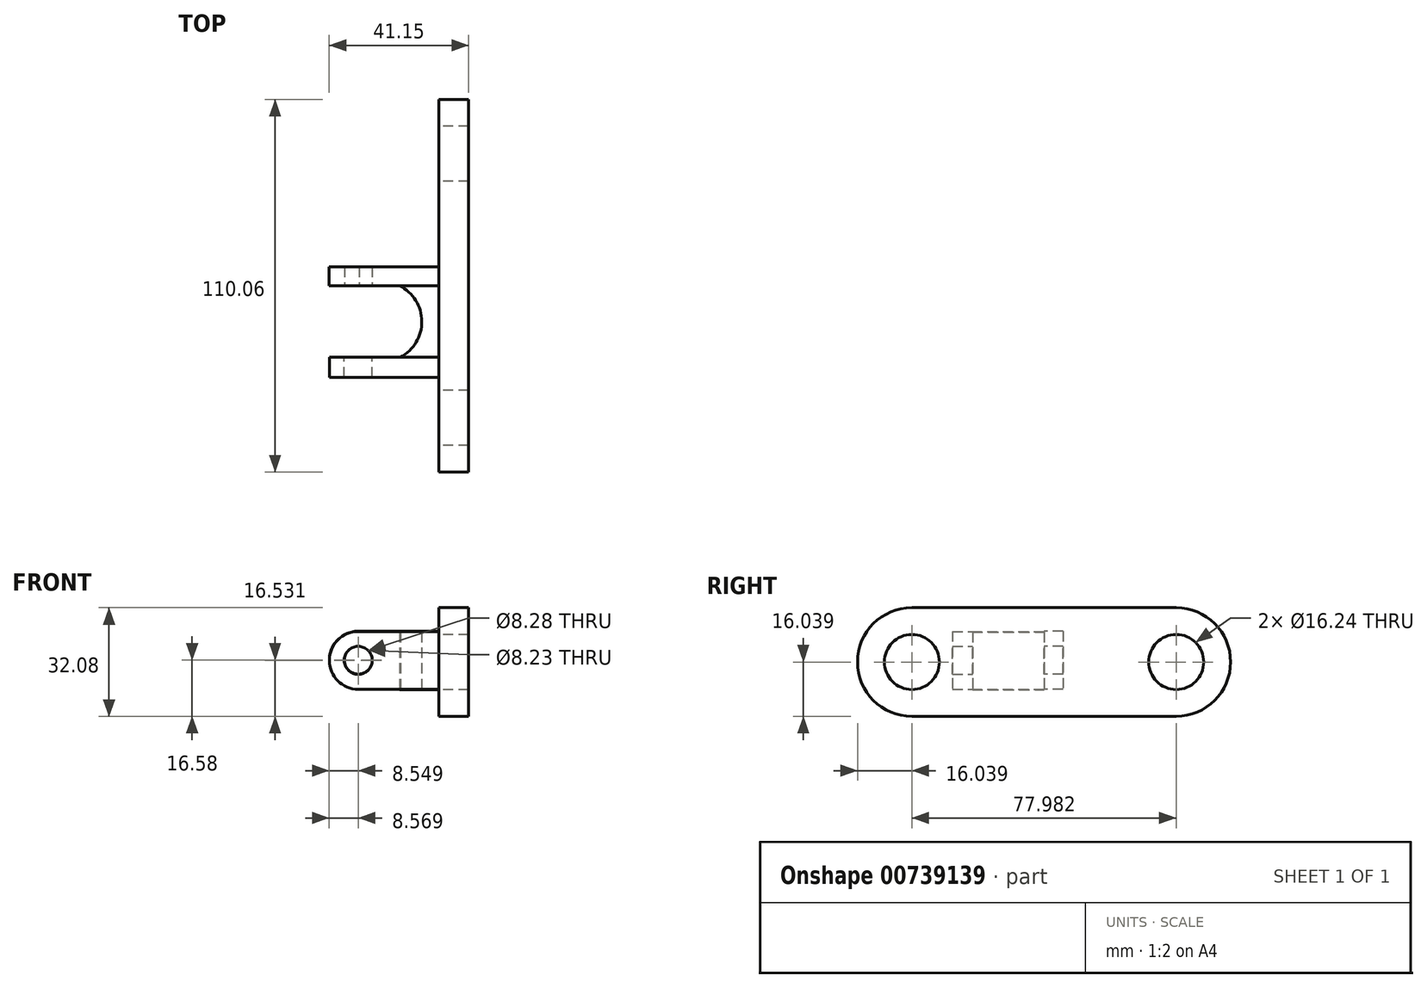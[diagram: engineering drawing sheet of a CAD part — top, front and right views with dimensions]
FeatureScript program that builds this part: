
annotation { "Feature Type Name" : "Feature", "Feature Type Description" : "" }
export const myFeature = defineFeature(function(context is Context, id is Id, definition is map)
    precondition{}
    {
        {
            var Q0;
            Q0=qCreatedBy(makeId("Right.planeOp"),FACE);
            var sketch = newSketch(context, id + "F0", { "sketchPlane" : qUnion([Q0])});
            skLineSegment(sketch, "E0", {"start": v(0, -16.5) * mm, "end": v(39, -16.5) * mm});
            skLineSegment(sketch, "E1", {"start": v(0, -16.5) * mm, "end": v(-39, -16.5) * mm});
            skLineSegment(sketch, "E2", {"start": v(39, 15.58) * mm, "end": v(-39, 15.58) * mm});
            skArc(sketch, "E3", {"start": v(39, -16.5) * mm, "mid": v(55.03, -0.46) * mm, "end": v(39, 15.58) * mm});
            skArc(sketch, "E4", {"start": v(-39, 15.58) * mm, "mid": v(-55.03, -0.46) * mm, "end": v(-39, -16.5) * mm});
            skCircle(sketch, "E5", {"center": v(39, -0.46) * mm, "radius": 8.12 * mm});
            skCircle(sketch, "E6", {"center": v(-39, -0.46) * mm, "radius": 8.12 * mm});
            skSolve(sketch);
        }
        {
            var Q0;
            Q0=makeQuery(id+"F0.imprint","IMPRINT",FACE,{"disambiguationData":[TD([[makeQuery(id+"F0.imprint","IMPRINT",EDGE,{"derivedFrom":sQuery(id+"F0.wireOp",EDGE,"E0")}),1.0]])]});
            extrude(context, id + "F1", {"entities" : qUnion([Q0]), "depth" : 8.9 * mm, "offsetDistance" : 25.4 * mm});
        }
        {
            var Q0;
            Q0=qCreatedBy(makeId("Front.planeOp"),FACE);
            cPlane(context, id + "F2", {"entities" : qUnion([Q0]), "cplaneType" : CPlaneType.OFFSET, "offset" : 21.08 * mm, "width" : 152.4 * mm, "height" : 152.4 * mm});
        }
        {
            var Q0;
            Q0=qCreatedBy(makeId("Top.planeOp"),FACE);
            var sketch = newSketch(context, id + "F3", { "sketchPlane" : qUnion([Q0])});
            skArc(sketch, "E7", {"start": v(-11.28, -21.09) * mm, "mid": v(-4.96, -10.49) * mm, "end": v(-11.47, 0) * mm});
            skLineSegment(sketch, "E8", {"start": v(-11.47, 0) * mm, "end": v(0, 0) * mm});
            skLineSegment(sketch, "E9", {"start": v(0, 0) * mm, "end": v(0, -21.17) * mm});
            skLineSegment(sketch, "E10", {"start": v(0, -21.17) * mm, "end": v(-11.28, -21.09) * mm});
            skSolve(sketch);
        }
        {
            var Q0;
            Q0=qCreatedBy(id+"F2.planeOp",FACE);
            var sketch = newSketch(context, id + "F4", { "sketchPlane" : qUnion([Q0])});
            skLineSegment(sketch, "E11", {"start": v(0, 8.56) * mm, "end": v(-23.79, 8.56) * mm});
            skLineSegment(sketch, "E12", {"start": v(0, 8.56) * mm, "end": v(0, -8.5) * mm});
            skLineSegment(sketch, "E13", {"start": v(0, -8.5) * mm, "end": v(-23.71, -8.5) * mm});
            skArc(sketch, "E14", {"start": v(-23.79, 8.56) * mm, "mid": v(-32.24, 0) * mm, "end": v(-23.71, -8.5) * mm});
            skCircle(sketch, "E15", {"center": v(-23.71, 0.03) * mm, "radius": 4.14 * mm});
            skSolve(sketch);
        }
        {
            var Q0;
            Q0 = qSketchRegion(id + "F4", true);
            extrude(context, id + "F5", {"entities" : qUnion([Q0]), "operationType" : NewBodyOperationType.ADD, "depth" : 5.92 * mm, "offsetDistance" : 25.4 * mm});
        }
        {
            var Q0;
            Q0=qCreatedBy(makeId("Front.planeOp"),FACE);
            var sketch = newSketch(context, id + "F6", { "sketchPlane" : qUnion([Q0])});
            skLineSegment(sketch, "E16", {"start": v(0, 8.65) * mm, "end": v(0, -8.48) * mm});
            skLineSegment(sketch, "E17", {"start": v(0, -8.48) * mm, "end": v(-23.47, -8.48) * mm});
            skLineSegment(sketch, "E18", {"start": v(0, 8.65) * mm, "end": v(-23.7, 8.65) * mm});
            skArc(sketch, "E19", {"start": v(-23.7, 8.65) * mm, "mid": v(-32.26, -0.03) * mm, "end": v(-23.47, -8.48) * mm});
            skCircle(sketch, "E20", {"center": v(-23.7, 0.08) * mm, "radius": 4.11 * mm});
            skSolve(sketch);
        }
        {
            var Q0;
            Q0=makeQuery(id+"F6.imprint","IMPRINT",FACE,{"disambiguationData":[TD([[makeQuery(id+"F6.imprint","IMPRINT",EDGE,{"derivedFrom":sQuery(id+"F6.wireOp",EDGE,"E17")}),-1.0]])]});
            extrude(context, id + "F7", {"entities" : qUnion([Q0]), "operationType" : NewBodyOperationType.ADD, "oppositeDirection" : true, "depth" : 5.6 * mm, "offsetDistance" : 25.4 * mm});
        }
        {
            var Q0;
            Q0=makeQuery(id+"F3.imprint","IMPRINT",FACE,{"disambiguationData":[TD([[makeQuery(id+"F3.imprint","IMPRINT",EDGE,{"derivedFrom":sQuery(id+"F3.wireOp",EDGE,"E7")}),-1.0]])]});
            extrude(context, id + "F8", {"entities" : qUnion([Q0]), "operationType" : NewBodyOperationType.ADD, "depth" : 8.38 * mm, "offsetDistance" : 25.4 * mm});
        }
        {
            var Q0;
            Q0=makeQuery(id+"F8.opExtrude","CAP_FACE",FACE,{"disambiguationData":[OSD([sQuery(id+"F3.wireOp",EDGE,"E7"),sQuery(id+"F3.wireOp",EDGE,"E8"),sQuery(id+"F3.wireOp",EDGE,"E9"),sQuery(id+"F3.wireOp",EDGE,"E10")])],"isStart":true});
            extrude(context, id + "F9", {"entities" : qUnion([Q0]), "operationType" : NewBodyOperationType.ADD, "depth" : 8.6 * mm, "offsetDistance" : 25.4 * mm});
        }
    });
